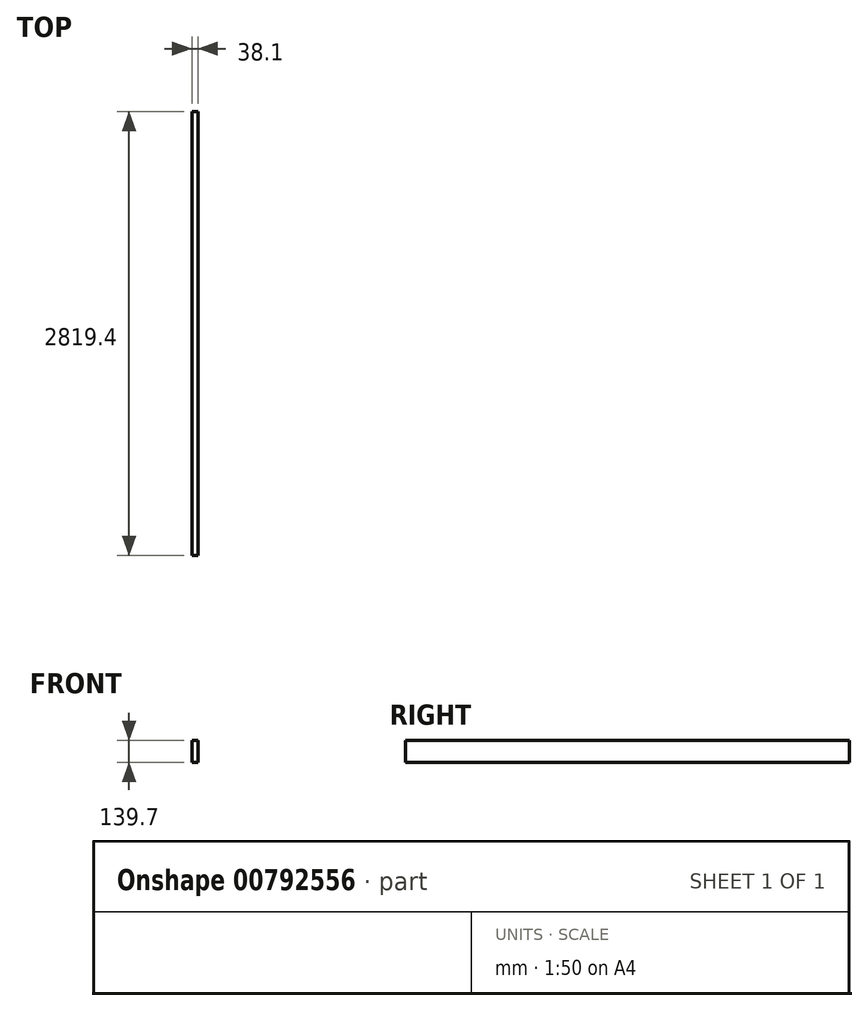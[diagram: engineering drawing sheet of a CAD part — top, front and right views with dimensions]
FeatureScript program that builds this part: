
annotation { "Feature Type Name" : "Feature", "Feature Type Description" : "" }
export const myFeature = defineFeature(function(context is Context, id is Id, definition is map)
    precondition{}
    {
        {
            var Q0;
            Q0=qCreatedBy(makeId("Front.planeOp"),FACE);
            var sketch = newSketch(context, id + "F0", { "sketchPlane" : qUnion([Q0])});
            skLineSegment(sketch, "E0.bottom", {"start": v(-19.05, -69.85) * mm, "end": v(19.05, -69.85) * mm});
            skLineSegment(sketch, "E0.top", {"start": v(-19.05, 69.85) * mm, "end": v(19.05, 69.85) * mm});
            skLineSegment(sketch, "E0.left", {"start": v(-19.05, -69.85) * mm, "end": v(-19.05, 69.85) * mm});
            skLineSegment(sketch, "E0.right", {"start": v(19.05, -69.85) * mm, "end": v(19.05, 69.85) * mm});
            skPoint(sketch, "E0.middle", {"position": v(0, 0) * mm});
            skSolve(sketch);
        }
        {
            var Q0;
            Q0=makeQuery(id+"F0.imprint","IMPRINT",FACE,{"disambiguationData":[TD([[makeQuery(id+"F0.imprint","IMPRINT",EDGE,{"derivedFrom":sQuery(id+"F0.wireOp",EDGE,"E0.bottom")}),1.0]])]});
            extrude(context, id + "F1", {"entities" : qUnion([Q0]), "endBound" : BoundingType.SYMMETRIC, "depth" : 2819.4 * mm, "offsetDistance" : 25.4 * mm});
        }
    });
